# Revit family: QF_BOURGEAT_chariot_cafeteria_18plateaux_modele_bas_couleur
name_source: partatom
category: Equipement spécialisé
revit_build: Autodesk Revit 2015 (Build: 20140606_1530(x64)
units: mm (PartAtom-declared; Revit-internal decimal feet)

## types (4) — shared parameters
Charge max = 90.00 kg
Fabricant = BOURGEAT
Hauteur hors tout = 994 mm
Longueur hors tout = 1337 mm  [stored 4.38648 ft]
Profondeur hors tout = 618 mm  [stored 2.02756 ft]
Spécification du Fabricant = CHARIOT CAFETERIA
URL catalogue = http://www.bourgeat.fr

## per-type parameters (varying)
| type | Modèle | Poids net à vide | panneaux_bleus | panneaux_rouges | panneaux_verts |
| chariot_modele_bas_glissieres_beiges_sans_panneaux | 782436 | 25.00 kg | Non | Non | Non |
| chariot_modele_bas_glissieres_beiges_avec_2panneaux_bleus | 782536 | 27.50 kg | Oui | Non | Non |
| chariot_modele_bas_glissieres_beiges_avec_2panneaux_rouges | 782736 | 27.50 kg | Non | Oui | Non |
| chariot_modele_bas_glissieres_beiges_avec_2panneaux_verts | 782636 | 27.50 kg | Non | Non | Oui |

note: [stored X ft] marks values corroborated as IEEE doubles in the binary element streams (Revit-internal decimal feet)
